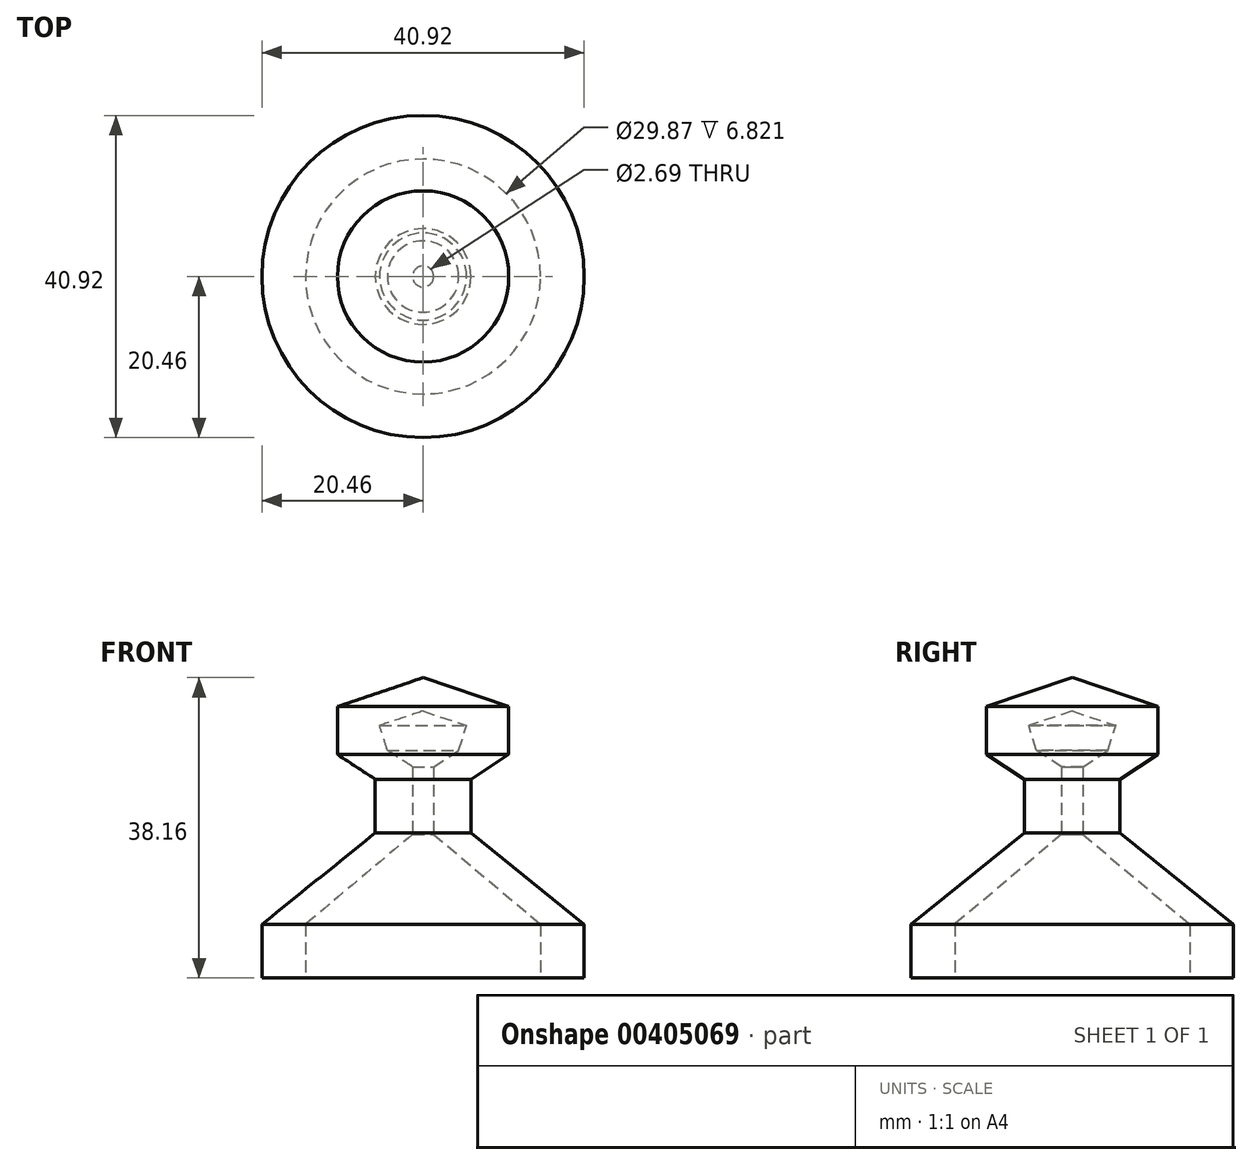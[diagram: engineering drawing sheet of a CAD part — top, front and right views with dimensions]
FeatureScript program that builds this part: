
annotation { "Feature Type Name" : "Feature", "Feature Type Description" : "" }
export const myFeature = defineFeature(function(context is Context, id is Id, definition is map)
    precondition{}
    {
        {
            var Q0;
            Q0=qCreatedBy(makeId("Right.planeOp"),FACE);
            var sketch = newSketch(context, id + "F0", { "sketchPlane" : qUnion([Q0])});
            skLineSegment(sketch, "E0", {"start": v(-20.46, 0) * mm, "end": v(-20.46, 6.82) * mm});
            skLineSegment(sketch, "E1", {"start": v(-20.46, 6.82) * mm, "end": v(-6.08, 18.44) * mm});
            skLineSegment(sketch, "E2", {"start": v(-6.08, 18.44) * mm, "end": v(-6.08, 25.26) * mm});
            skLineSegment(sketch, "E3", {"start": v(-6.08, 25.26) * mm, "end": v(-10.88, 28.4) * mm});
            skLineSegment(sketch, "E4", {"start": v(-10.88, 28.4) * mm, "end": v(-10.88, 34.47) * mm});
            skLineSegment(sketch, "E5", {"start": v(-10.88, 34.47) * mm, "end": v(0, 38.16) * mm});
            skLineSegment(sketch, "E6", {"start": v(0, 38.16) * mm, "end": v(0, 33.92) * mm});
            skLineSegment(sketch, "E7", {"start": v(-4.53, 28.93) * mm, "end": v(-1.34, 26.85) * mm});
            skLineSegment(sketch, "E8", {"start": v(-1.34, 26.85) * mm, "end": v(-1.34, 18.25) * mm});
            skLineSegment(sketch, "E9", {"start": v(-1.34, 18.25) * mm, "end": v(-14.93, 6.82) * mm});
            skLineSegment(sketch, "E10", {"start": v(-14.93, 6.82) * mm, "end": v(-14.93, 0) * mm});
            skLineSegment(sketch, "E11", {"start": v(-14.93, 0) * mm, "end": v(-20.46, 0) * mm});
            skLineSegment(sketch, "E12", {"start": v(0, 33.92) * mm, "end": v(-5.53, 32.08) * mm});
            skLineSegment(sketch, "E13", {"start": v(-5.53, 32.08) * mm, "end": v(-4.53, 28.93) * mm});
            skLineSegment(sketch, "E14", {"start": v(0, 45.35) * mm, "end": v(0, 0) * mm});
            skSolve(sketch);
        }
        {
            var Q0;
            Q0=sQuery(id+"F0.wireOp",EDGE,"E5");
            var Q1;
            Q1=sQuery(id+"F0.wireOp",EDGE,"E4");
            var Q2;
            Q2=sQuery(id+"F0.wireOp",EDGE,"E3");
            var Q3;
            Q3=sQuery(id+"F0.wireOp",EDGE,"E2");
            var Q4;
            Q4=sQuery(id+"F0.wireOp",EDGE,"E1");
            var Q5;
            Q5=sQuery(id+"F0.wireOp",EDGE,"E0");
            var Q6;
            Q6=sQuery(id+"F0.wireOp",EDGE,"E11");
            var Q7;
            Q7=sQuery(id+"F0.wireOp",EDGE,"E10");
            var Q8;
            Q8=sQuery(id+"F0.wireOp",EDGE,"E9");
            var Q9;
            Q9=sQuery(id+"F0.wireOp",EDGE,"E8");
            var Q10;
            Q10=sQuery(id+"F0.wireOp",EDGE,"E7");
            var Q11;
            Q11=sQuery(id+"F0.wireOp",EDGE,"E13");
            var Q12;
            Q12=sQuery(id+"F0.wireOp",EDGE,"E12");
            var Q13;
            Q13=sQuery(id+"F0.wireOp",EDGE,"E14");
            revolve(context, id + "F1", {"bodyType" : ToolBodyType.SURFACE, "surfaceEntities" : qUnion([Q0, Q1, Q2, Q3, Q4, Q5, Q6, Q7, Q8, Q9, Q10, Q11, Q12]), "axis" : qUnion([Q13]), "revolveType" : RevolveType.FULL});
        }
    });
